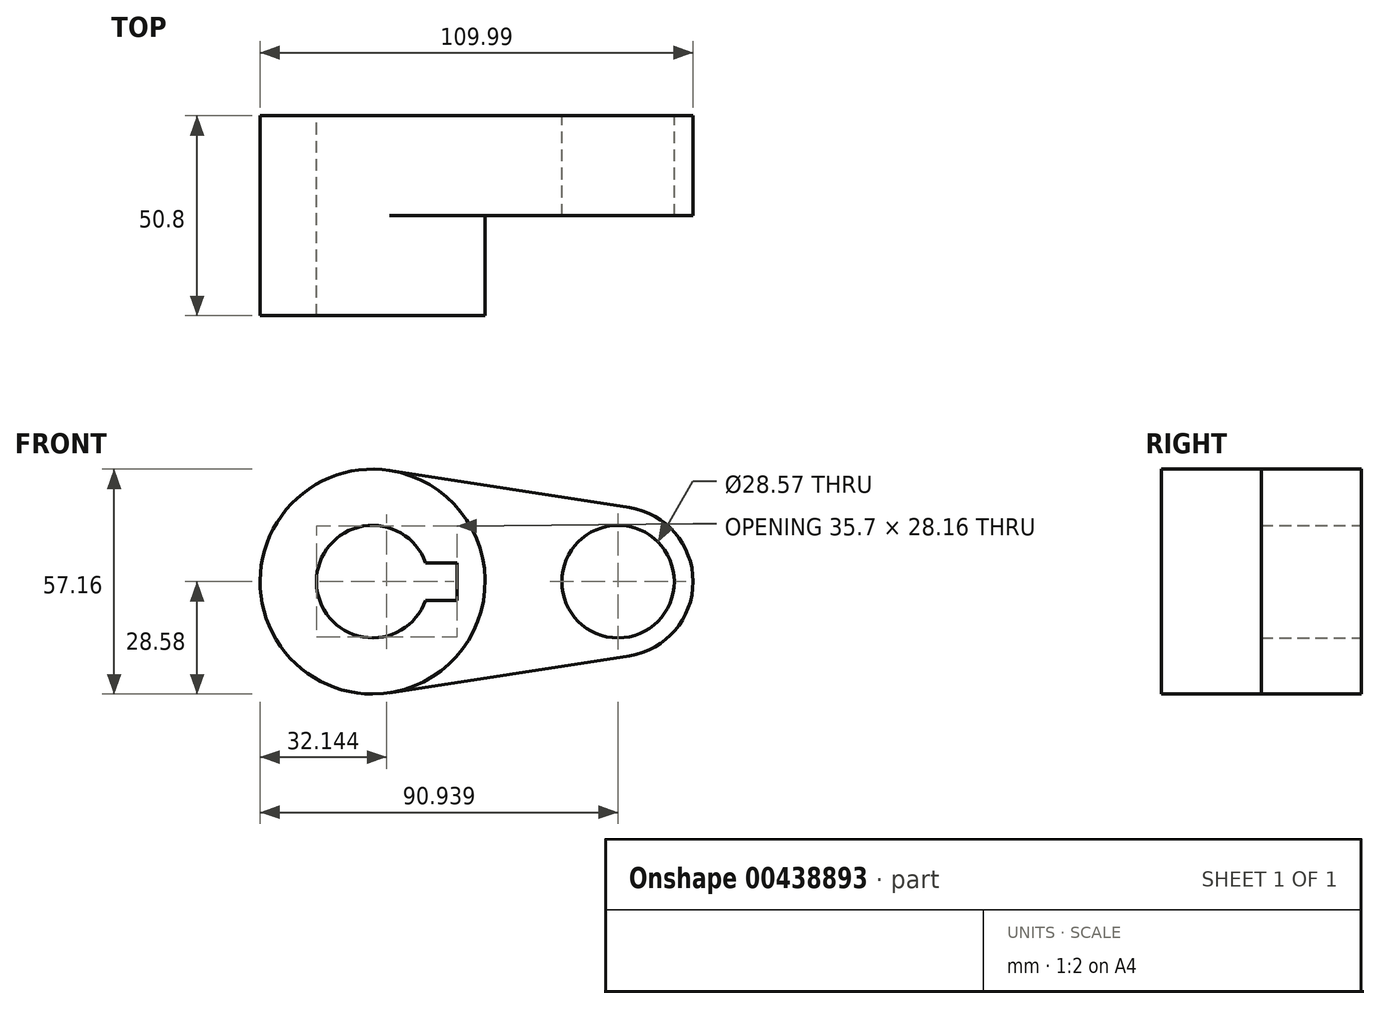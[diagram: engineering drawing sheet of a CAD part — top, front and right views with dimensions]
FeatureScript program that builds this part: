
annotation { "Feature Type Name" : "Feature", "Feature Type Description" : "" }
export const myFeature = defineFeature(function(context is Context, id is Id, definition is map)
    precondition{}
    {
        {
            var Q0;
            Q0=qCreatedBy(makeId("Front.planeOp"),FACE);
            var sketch = newSketch(context, id + "F0", { "sketchPlane" : qUnion([Q0])});
            skCircle(sketch, "E0", {"center": v(0, 0) * mm, "radius": 28.58 * mm});
            skCircle(sketch, "E1", {"center": v(62.36, 0) * mm, "radius": 19.05 * mm});
            skCircle(sketch, "E2", {"center": v(0, 0) * mm, "radius": 14.29 * mm});
            skCircle(sketch, "E3", {"center": v(62.36, 0) * mm, "radius": 14.29 * mm});
            skLineSegment(sketch, "E4.bottom", {"start": v(21.41, 4.76) * mm, "end": v(-21.41, 4.76) * mm});
            skLineSegment(sketch, "E4.top", {"start": v(21.41, -4.76) * mm, "end": v(-21.41, -4.76) * mm});
            skLineSegment(sketch, "E4.left", {"start": v(21.41, 4.76) * mm, "end": v(21.41, -4.76) * mm});
            skLineSegment(sketch, "E4.right", {"start": v(-21.41, 4.76) * mm, "end": v(-21.41, -4.76) * mm});
            skLineSegment(sketch, "E5", {"start": v(4.36, -28.24) * mm, "end": v(65.27, -18.83) * mm});
            skLineSegment(sketch, "E6", {"start": v(4.36, 28.24) * mm, "end": v(65.27, 18.83) * mm});
            skSolve(sketch);
        }
        {
            var Q0;
            {var subQ5=sQuery(id+"F0.wireOp",EDGE,"E4.right");Q0=makeQuery(id+"F0.imprint","IMPRINT",FACE,{"disambiguationData":[TD([[makeQuery(id+"F0.imprint","IMPRINT",EDGE,{"derivedFrom":subQ5}),1.0]])]});}
            var Q1;
            {var subQ4=sQuery(id+"F0.wireOp",EDGE,"E4.left");Q1=makeQuery(id+"F0.imprint","IMPRINT",FACE,{"disambiguationData":[TD([[makeQuery(id+"F0.imprint","IMPRINT",EDGE,{"derivedFrom":subQ4}),1.0]])]});}
            extrude(context, id + "F1", {"entities" : qUnion([Q0, Q1]), "depth" : 50.8 * mm});
        }
        {
            var Q0;
            {var subQ0=sQuery(id+"F0.wireOp",EDGE,"E5");Q0=makeQuery(id+"F0.imprint","IMPRINT",FACE,{"disambiguationData":[TD([[makeQuery(id+"F0.imprint","IMPRINT",EDGE,{"derivedFrom":subQ0}),1.0]])]});}
            var Q1;
            Q1=makeQuery(id+"F0.imprint","IMPRINT",FACE,{"disambiguationData":[TD([[makeQuery(id+"F0.imprint","IMPRINT",EDGE,{"derivedFrom":sQuery(id+"F0.wireOp",EDGE,"E3")}),-1.0]])]});
            extrude(context, id + "F2", {"entities" : qUnion([Q0, Q1]), "operationType" : NewBodyOperationType.ADD, "depth" : 25.4 * mm});
        }
    });
